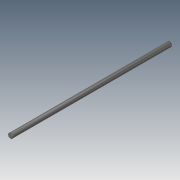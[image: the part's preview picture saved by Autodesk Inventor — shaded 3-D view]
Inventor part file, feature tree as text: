
AUTODESK INVENTOR PART (.ipt)
format: ipt  version: 2018.2 (Build 222227000, 227)  size: 80,896 bytes
history: native  units: mm
features: extrude x1, chamfer x1, sketch x1
ambient origin geometry x8: Origin, YZ Plane, XZ Plane, XY Plane, X Axis, Y Axis, Z Axis, Center Point
bodies: Body1 (feature_tree)
feature tree (3):
  extrude  "Grundkörper"  Depth=205.0mm TaperAngle=0.0deg
  chamfer  "Fase1"  Distance=10.0mm
  sketch  "Skizze2"  dims[d5=6.0mm d6=205.0mm d7=0.0mm d8=10.0mm d9=0.0mm d10=0.5mm d11=2.0mm d12=45.0deg]
